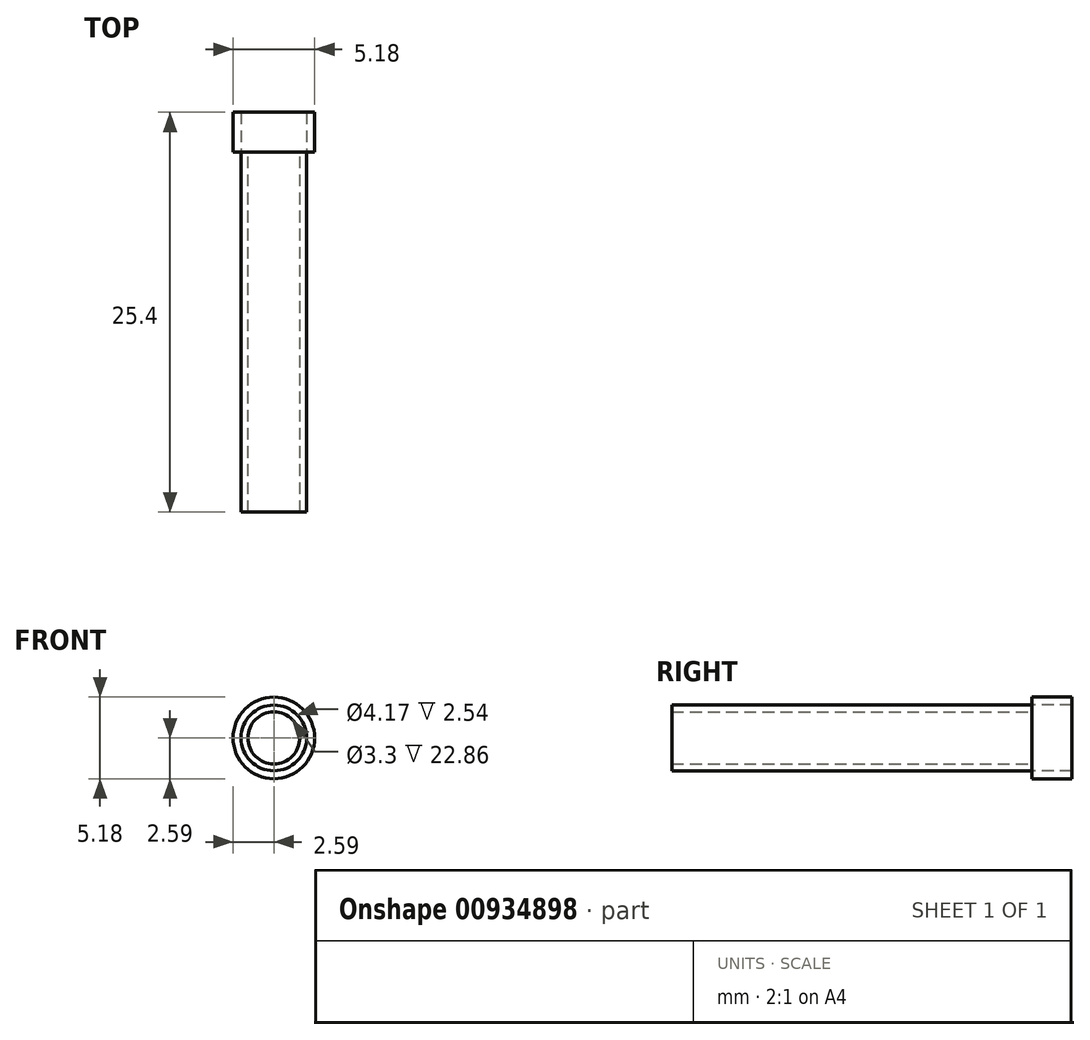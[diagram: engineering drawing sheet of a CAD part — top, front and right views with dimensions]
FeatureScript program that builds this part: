
annotation { "Feature Type Name" : "Feature", "Feature Type Description" : "" }
export const myFeature = defineFeature(function(context is Context, id is Id, definition is map)
    precondition{}
    {
        {
            var Q0;
            Q0=qCreatedBy(makeId("Front.planeOp"),FACE);
            var sketch = newSketch(context, id + "F0", { "sketchPlane" : qUnion([Q0])});
            skCircle(sketch, "E0", {"center": v(0, 0) * mm, "radius": 2.59 * mm});
            skCircle(sketch, "E1", {"center": v(0, 0) * mm, "radius": 2.09 * mm});
            skCircle(sketch, "E2", {"center": v(0, 0) * mm, "radius": 1.65 * mm});
            skSolve(sketch);
        }
        {
            var Q0;
            Q0=makeQuery(id+"F0.imprint","IMPRINT",FACE,{"disambiguationData":[TD([[makeQuery(id+"F0.imprint","IMPRINT",EDGE,{"derivedFrom":sQuery(id+"F0.wireOp",EDGE,"E1")}),1.0]])]});
            var Q1;
            Q1=sQuery(id+"F0.wireOp",EDGE,"E2");
            var Q2;
            Q2=sQuery(id+"F0.wireOp",EDGE,"E1");
            extrude(context, id + "F1", {"entities" : qUnion([Q0]), "surfaceEntities" : qUnion([Q1, Q2]), "depth" : 22.86 * mm, "offsetDistance" : 25.4 * mm});
        }
        {
            var Q0;
            Q0=makeQuery(id+"F0.imprint","IMPRINT",FACE,{"disambiguationData":[TD([[makeQuery(id+"F0.imprint","IMPRINT",EDGE,{"derivedFrom":sQuery(id+"F0.wireOp",EDGE,"E1")}),1.0]])]});
            var sketch = newSketch(context, id + "F2", { "sketchPlane" : qUnion([Q0])});
            skCircle(sketch, "E3", {"center": v(0, 0) * mm, "radius": 2.47 * mm});
            skSolve(sketch);
        }
        {
            var Q0;
            Q0=makeQuery(id+"F0.imprint","IMPRINT",FACE,{"disambiguationData":[TD([[makeQuery(id+"F0.imprint","IMPRINT",EDGE,{"derivedFrom":sQuery(id+"F0.wireOp",EDGE,"E0")}),1.0]])]});
            var Q1;
            Q1=sQuery(id+"F2.wireOp",EDGE,"E3");
            extrude(context, id + "F3", {"entities" : qUnion([Q0]), "surfaceEntities" : qUnion([Q1]), "oppositeDirection" : true, "depth" : 2.54 * mm, "offsetDistance" : 25.4 * mm});
        }
    });
